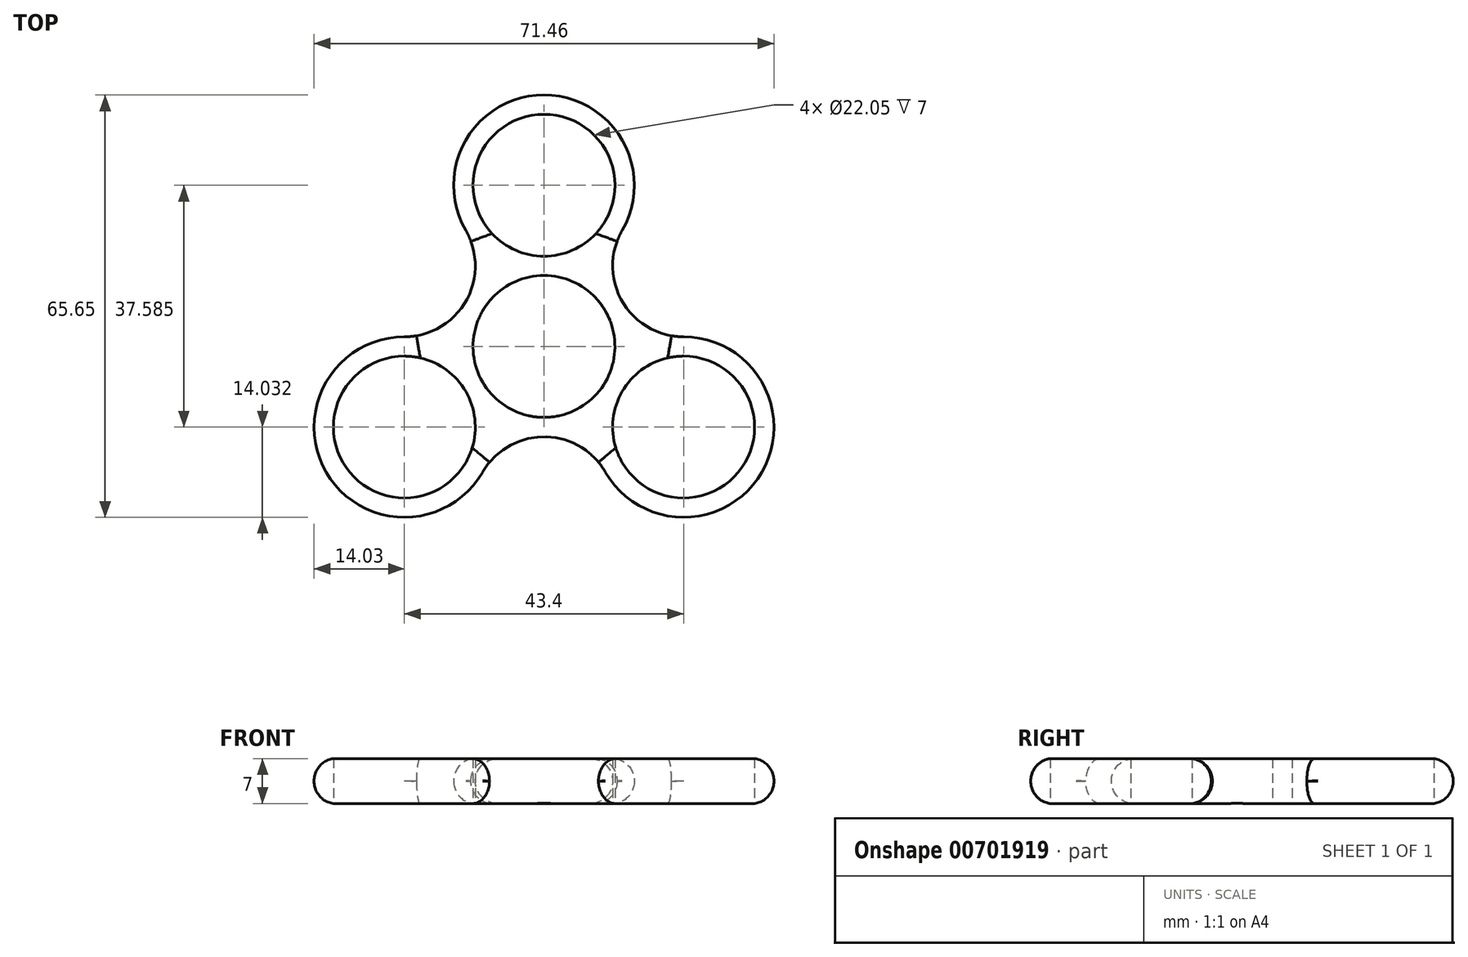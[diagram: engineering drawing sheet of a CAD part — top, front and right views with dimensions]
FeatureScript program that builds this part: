
annotation { "Feature Type Name" : "Feature", "Feature Type Description" : "" }
export const myFeature = defineFeature(function(context is Context, id is Id, definition is map)
    precondition{}
    {
        {
            var Q0;
            Q0=qCreatedBy(makeId("Top.planeOp"),FACE);
            var sketch = newSketch(context, id + "F0", { "sketchPlane" : qUnion([Q0])});
            skCircle(sketch, "E0", {"center": v(0, 0) * mm, "radius": 39.09 * mm, "construction": true});
            skCircle(sketch, "E1", {"center": v(0, 0) * mm, "radius": 25.06 * mm, "construction": true});
            skCircle(sketch, "E2", {"center": v(0, 0) * mm, "radius": 11.03 * mm});
            skCircle(sketch, "E3", {"center": v(0, 25.06) * mm, "radius": 11.03 * mm});
            skArc(sketch, "E4.1.0", {"start": v(-21.7, 1.5) * mm, "mid": v(-12.15, 7.02) * mm, "end": v(-12.15, 18.04) * mm});
            skCircle(sketch, "E4.2.0", {"center": v(-21.7, -12.53) * mm, "radius": 11.03 * mm});
            skArc(sketch, "E4.3.0", {"start": v(9.55, -19.54) * mm, "mid": v(0, -14.03) * mm, "end": v(-9.55, -19.54) * mm});
            skCircle(sketch, "E4.4.0", {"center": v(21.7, -12.53) * mm, "radius": 11.03 * mm});
            skArc(sketch, "E4.5.0", {"start": v(12.15, 18.04) * mm, "mid": v(12.15, 7.02) * mm, "end": v(21.7, 1.5) * mm});
            skArc(sketch, "E5", {"start": v(12.15, 18.04) * mm, "mid": v(0, 39.09) * mm, "end": v(-12.15, 18.04) * mm});
            skArc(sketch, "E6", {"start": v(-21.7, 1.5) * mm, "mid": v(-33.85, -19.54) * mm, "end": v(-9.55, -19.54) * mm});
            skArc(sketch, "E7", {"start": v(9.55, -19.54) * mm, "mid": v(33.85, -19.54) * mm, "end": v(21.7, 1.5) * mm});
            skSolve(sketch);
        }
        {
            var Q0;
            Q0=makeQuery(id+"F0.imprint","IMPRINT",FACE,{"disambiguationData":[TD([[makeQuery(id+"F0.imprint","IMPRINT",EDGE,{"derivedFrom":sQuery(id+"F0.wireOp",EDGE,"E2")}),-1.0]])]});
            extrude(context, id + "F1", {"entities" : qUnion([Q0]), "depth" : 7 * mm, "offsetDistance" : 25 * mm});
        }
        {
            var Q0;
            Q0=makeQuery(id+"F1.opExtrude","SWEPT_FACE",FACE,{"disambiguationData":[OSD([sQuery(id+"F0.wireOp",EDGE,"E5")])]});
            fillet(context, id + "F2", {"entities" : qUnion([Q0]), "radius" : 3.5 * mm, "tangentPropagation" : true, "allowEdgeOverflow" : false});
        }
    });
